# Revit family: Heavy Timber-Section
name_source: partatom
category: Detail Items
revit_build: Autodesk Revit Architecture 2012 (Build: 20110210_1515)
units: mm (PartAtom-declared; Revit-internal decimal feet)

## types (28) — shared parameters

## per-type parameters (varying)
| type | Depth | Keynote | Width |
| 4x4 | 0' - 3 1/2" | 06 13 23.A1 | 0' - 3 1/2" |
| 4x6 | 0' - 5 1/2" | 06 13 23.A2 | 0' - 3 1/2" |
| 4x8 | 0' - 7 1/4" | 06 13 23.A3 | 0' - 3 1/2" |
| 4x10 | 0' - 9 1/4" | 06 13 23.A4 | 0' - 3 1/2" |
| 4x12 | 0' - 11 1/4" | 06 13 23.A5 | 0' - 3 1/2" |
| 4x14 | 1' - 1 1/2" | 06 13 23.A6 | 0' - 3 1/2" |
| 4x16 | 1' - 3 1/2" | 06 13 23.A7 | 0' - 3 1/2" |
| 6x6 | 0' - 5 1/2" | 06 13 23.B1 | 0' - 5 1/2" |
| 6x8 | 0' - 7 1/4" | 06 13 23.B2 | 0' - 5 1/2" |
| 6x10 | 0' - 9 1/4" | 06 13 23.B3 | 0' - 5 1/2" |
| 6x12 | 0' - 11 1/4" | 06 13 23.B4 | 0' - 5 1/2" |
| 6x14 | 1' - 1 1/2" | 06 13 23.B5 | 0' - 5 1/2" |
| 6x16 | 1' - 3 1/2" | 06 13 23.B6 | 0' - 5 1/2" |
| 8x8 | 0' - 7 1/4" | 06 13 23.C1 | 0' - 7 1/4" |
| 8x10 | 0' - 9 1/4" | 06 13 23.C2 | 0' - 7 1/4" |
| 8x12 | 0' - 11 1/4" | 06 13 23.C3 | 0' - 7 1/4" |
| 8x14 | 1' - 1 1/2" | 06 13 23.C4 | 0' - 7 1/4" |
| 8x16 | 1' - 3 1/2" | 06 13 23.C5 | 0' - 7 1/4" |
| 10x10 | 0' - 9 1/4" | 06 13 23.D1 | 0' - 9 1/4" |
| 10x12 | 0' - 11 1/4" | 06 13 23.D2 | 0' - 9 1/4" |
| 10x14 | 1' - 1 1/2" | 06 13 23.D3 | 0' - 9 1/4" |
| 10x16 | 1' - 3 1/2" | 06 13 23.D4 | 0' - 9 1/4" |
| 12x12 | 0' - 11 1/4" | 06 13 23.E1 | 0' - 11 1/4" |
| 12x14 | 1' - 1 1/2" | 06 13 23.E2 | 0' - 11 1/4" |
| 12x16 | 1' - 3 1/2" | 06 13 23.E3 | 0' - 11 1/4" |
| 14x14 | 1' - 1 1/2" | 06 13 23.F1 | 1' - 1 1/4" |
| 14x16 | 1' - 3 1/2" | 06 13 23.F2 | 1' - 1 1/4" |
| 16x16 | 1' - 3 1/2" | 06 13 23.G1 | 1' - 3 1/4" |
